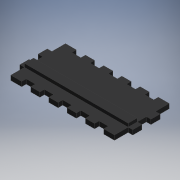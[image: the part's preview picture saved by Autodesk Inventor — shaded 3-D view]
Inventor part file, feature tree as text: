
AUTODESK INVENTOR PART (.ipt)
format: ipt  version: 2019 (Build 230136000, 136)  size: 207,360 bytes
history: native  units: mm
features: extrude x3, sketch x3
ambient origin geometry x8: Origin, YZ Plane, XZ Plane, XY Plane, X Axis, Y Axis, Z Axis, Center Point
bodies: Solid1 (feature_tree)
feature tree (6):
  extrude  "Extrusion1"  Depth=48.0mm
  extrude  "Extrusion2"  Depth=4.0mm
  extrude  "Extrusion3"  Depth=4.0mm
  sketch  "Sketch1"  dims[d0=99.0mm d1=48.0mm]
  sketch  "Sketch2"  dims[d6=4.0mm d7=0.0mm d8=4.0mm]
  sketch  "Sketch3"  dims[d11=8.0mm d12=4.0mm d14=8.0mm d15=8.0mm d16=8.0mm d17=4.0mm d18=8.0mm d19=4.0mm d20=0.0mm d21=8.0mm d22=8.0mm d23=3.0mm d24=0.0mm]
